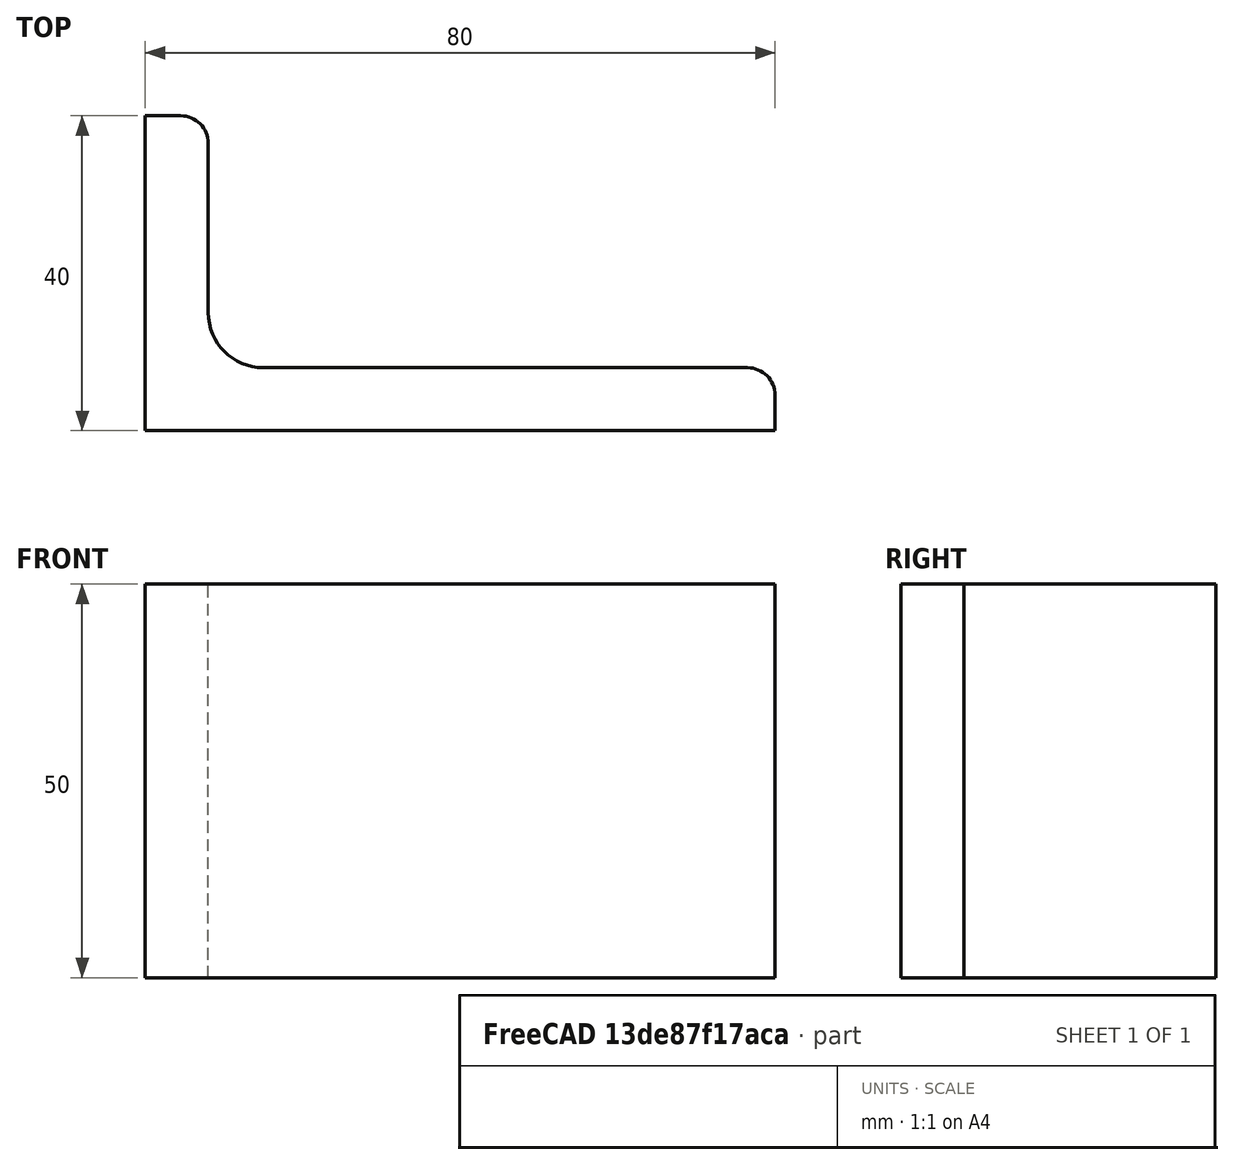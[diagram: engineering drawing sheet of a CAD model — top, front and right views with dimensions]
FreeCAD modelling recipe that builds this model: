
FCSTD DOCUMENT  (FreeCAD 0.15R4671 (Git))
Label: Angle Bar 80x40x8 EN10056 S235JR
License: All rights reserved
LicenseURL: http://en.wikipedia.org/wiki/All_rights_reserved
objects: Sketcher::SketchObject×1, Part::Extrusion×1
note: 2 computed .brp shape members not serialized (recipe doc carries the construction recipe); baked Part::Feature solids carry a one-line shape summary decoded from their .brp

FEATURE [Sketcher::SketchObject] Sketch
  sketch-geometry (9):
    g0: LineSegment StartX=0 StartY=0 StartZ=0 EndX=80 EndY=0 EndZ=0
    g1: LineSegment StartX=80 StartY=0 StartZ=0 EndX=80 EndY=4.5 EndZ=0
    g2: LineSegment StartX=76.5 StartY=8 StartZ=0 EndX=15 EndY=8 EndZ=0
    g3: LineSegment StartX=0 StartY=0 StartZ=0 EndX=0 EndY=40 EndZ=0
    g4: LineSegment StartX=0 StartY=40 StartZ=0 EndX=4.5 EndY=40 EndZ=0
    g5: LineSegment StartX=8 StartY=36.5 StartZ=0 EndX=8 EndY=15 EndZ=0
    g6: ArcOfCircle CenterX=15 CenterY=15 CenterZ=0 NormalX=0 NormalY=0 NormalZ=1 Radius=7 StartAngle=3.14159 EndAngle=4.71239
    g7: ArcOfCircle CenterX=4.5 CenterY=36.5 CenterZ=0 NormalX=0 NormalY=0 NormalZ=1 Radius=3.5 StartAngle=0 EndAngle=1.5708
    g8: ArcOfCircle CenterX=76.5 CenterY=4.5 CenterZ=0 NormalX=0 NormalY=0 NormalZ=1 Radius=3.5 StartAngle=0 EndAngle=1.5708
  constraints (23):
    c: Coincident(g0,g-1)
    c: Horizontal(g0)
    c: Coincident(g1,g0)
    c: Vertical(g1)
    c: Horizontal(g2)
    c: Coincident(g3,g-1)
    c: Vertical(g3)
    c: Coincident(g4,g3)
    c: Horizontal(g4)
    c: Vertical(g5)
    c: Tangent(g5,g6) = -1.5708
    c: Tangent(g2,g6) = 1.5708
    c: Tangent(g4,g7) = 1.5708
    c: Tangent(g5,g7) = 1.5708
    c: Tangent(g2,g8) = -1.5708
    c: Tangent(g1,g8) = -1.5708
    c: DistanceX(g0) = 80
    c: DistanceY(g3) = 40
    c: DistanceY(g0,g2) = 8
    c: DistanceX(g3,g5) = 8
    c: Radius(g6) = 7
    c: Radius(g8) = 3.5
    c: Radius(g7) = 3.5
FEATURE [Part::Extrusion] Extrude  label="Angle Bar 80x40x8 EN10056 S235JR"
  Base = -> Sketch
  Dir = (0,0,50)
  Solid = true
